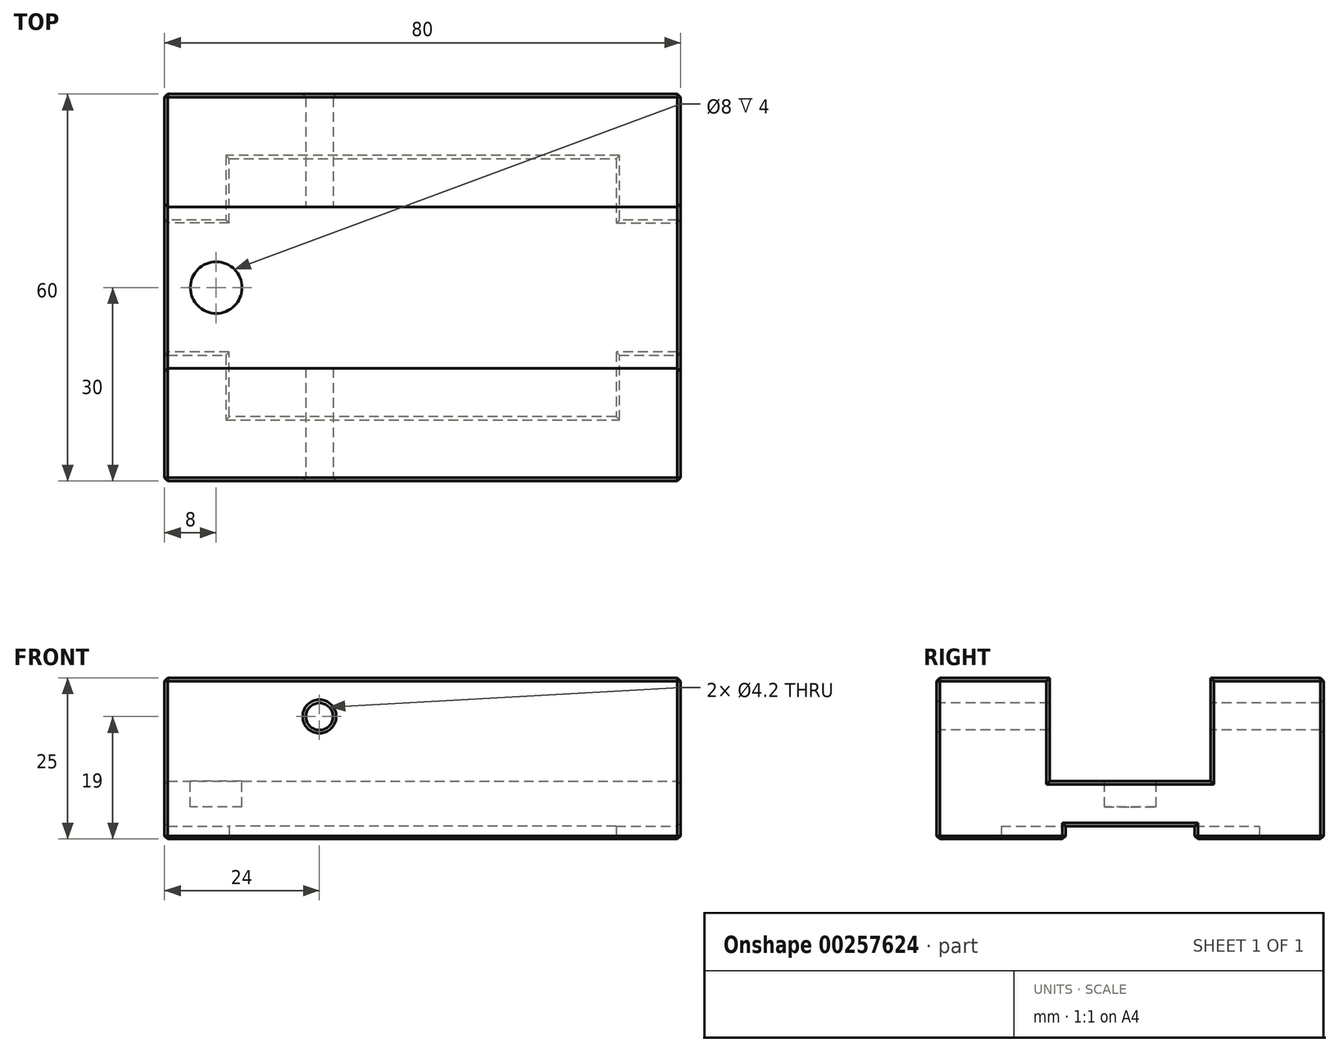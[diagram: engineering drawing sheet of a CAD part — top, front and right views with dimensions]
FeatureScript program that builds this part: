
annotation { "Feature Type Name" : "Feature", "Feature Type Description" : "" }
export const myFeature = defineFeature(function(context is Context, id is Id, definition is map)
    precondition{}
    {
        {
            var Q0;
            Q0=qCreatedBy(makeId("Top.planeOp"),FACE);
            var sketch = newSketch(context, id + "F0", { "sketchPlane" : qUnion([Q0])});
            skLineSegment(sketch, "E0.bottom", {"start": v(40, 30) * mm, "end": v(-40, 30) * mm});
            skLineSegment(sketch, "E0.top", {"start": v(40, -30) * mm, "end": v(-40, -30) * mm});
            skLineSegment(sketch, "E0.left", {"start": v(40, 30) * mm, "end": v(40, -30) * mm});
            skLineSegment(sketch, "E0.right", {"start": v(-40, 30) * mm, "end": v(-40, -30) * mm});
            skPoint(sketch, "E0.middle", {"position": v(0, 0) * mm});
            skSolve(sketch);
        }
        {
            var Q0;
            Q0 = qSketchRegion(id + "F0", true);
            extrude(context, id + "F1", {"entities" : qUnion([Q0]), "depth" : 25 * mm});
        }
        {
            var Q0;
            Q0=makeQuery(id+"F1.opExtrude","CAP_FACE",FACE,{"disambiguationData":[OSD([sQuery(id+"F0.wireOp",EDGE,"E0.bottom"),sQuery(id+"F0.wireOp",EDGE,"E0.top"),sQuery(id+"F0.wireOp",EDGE,"E0.left"),sQuery(id+"F0.wireOp",EDGE,"E0.right")])],"isStart":true});
            var sketch = newSketch(context, id + "F2", { "sketchPlane" : qUnion([Q0])});
            skLineSegment(sketch, "E1.bottom", {"start": v(30, 20) * mm, "end": v(-30, 20) * mm});
            skLineSegment(sketch, "E1.top", {"start": v(30, -20) * mm, "end": v(-30, -20) * mm});
            skLineSegment(sketch, "E1.left", {"start": v(30, 20) * mm, "end": v(30, 10) * mm});
            skLineSegment(sketch, "E1.right", {"start": v(-30, 20) * mm, "end": v(-30, 10) * mm});
            skPoint(sketch, "E1.middle", {"position": v(0, 0) * mm});
            skLineSegment(sketch, "E2", {"start": v(-30, -10) * mm, "end": v(-40, -10) * mm});
            skLineSegment(sketch, "E3", {"start": v(-40, -10) * mm, "end": v(-40, 10) * mm});
            skLineSegment(sketch, "E4", {"start": v(-40, 10) * mm, "end": v(-30, 10) * mm});
            skLineSegment(sketch, "E5.trimOffspring", {"start": v(-30, -10) * mm, "end": v(-30, -20) * mm});
            skLineSegment(sketch, "E6", {"start": v(-30, -10) * mm, "end": v(30, -10) * mm, "construction": true});
            skLineSegment(sketch, "E7", {"start": v(-30, 10) * mm, "end": v(30, 10) * mm, "construction": true});
            skLineSegment(sketch, "E8", {"start": v(30, -10) * mm, "end": v(40, -10) * mm});
            skLineSegment(sketch, "E9", {"start": v(40, -10) * mm, "end": v(40, 10) * mm});
            skLineSegment(sketch, "E10", {"start": v(40, 10) * mm, "end": v(30, 10) * mm});
            skLineSegment(sketch, "E11.trimOffspring", {"start": v(30, -10) * mm, "end": v(30, -20) * mm});
            skSolve(sketch);
        }
        {
            var Q0;
            Q0 = qSketchRegion(id + "F2", true);
            extrude(context, id + "F3", {"entities" : qUnion([Q0]), "operationType" : NewBodyOperationType.REMOVE, "oppositeDirection" : true, "depth" : 2 * mm});
        }
        {
            var Q0;
            Q0=makeQuery(id+"F1.opExtrude","CAP_FACE",FACE,{"disambiguationData":[OSD([sQuery(id+"F0.wireOp",EDGE,"E0.bottom"),sQuery(id+"F0.wireOp",EDGE,"E0.top"),sQuery(id+"F0.wireOp",EDGE,"E0.left"),sQuery(id+"F0.wireOp",EDGE,"E0.right")])],"isStart":false});
            var sketch = newSketch(context, id + "F4", { "sketchPlane" : qUnion([Q0])});
            skLineSegment(sketch, "E12.bottom", {"start": v(-40, -12.5) * mm, "end": v(40, -12.5) * mm});
            skLineSegment(sketch, "E12.top", {"start": v(-40, 12.5) * mm, "end": v(40, 12.5) * mm});
            skLineSegment(sketch, "E12.left", {"start": v(-40, -12.5) * mm, "end": v(-40, 12.5) * mm});
            skLineSegment(sketch, "E12.right", {"start": v(40, -12.5) * mm, "end": v(40, 12.5) * mm});
            skPoint(sketch, "E12.middle", {"position": v(0, 0) * mm});
            skSolve(sketch);
        }
        {
            var Q0;
            Q0=makeQuery(id+"F4.imprint","IMPRINT",FACE,{"disambiguationData":[TD([[makeQuery(id+"F4.imprint","IMPRINT",EDGE,{"derivedFrom":sQuery(id+"F4.wireOp",EDGE,"E12.bottom")}),1.0]])]});
            extrude(context, id + "F5", {"entities" : qUnion([Q0]), "operationType" : NewBodyOperationType.REMOVE, "oppositeDirection" : true, "depth" : 16 * mm});
        }
        {
            var Q0;
            Q0=makeQuery(id+"F5.boolean.opBoolean","COPY",FACE,{"derivedFrom":makeQuery(id+"F5.opExtrude","CAP_FACE",FACE,{"disambiguationData":[OSD([sQuery(id+"F4.wireOp",EDGE,"E12.bottom"),sQuery(id+"F4.wireOp",EDGE,"E12.top"),sQuery(id+"F4.wireOp",EDGE,"E12.left"),sQuery(id+"F4.wireOp",EDGE,"E12.right")])],"isStart":false})});
            var sketch = newSketch(context, id + "F6", { "sketchPlane" : qUnion([Q0])});
            skPoint(sketch, "E13", {"position": v(-32, 0) * mm});
            skCircle(sketch, "E14", {"center": v(-32, 0) * mm, "radius": 4 * mm});
            skSolve(sketch);
        }
        {
            var Q0;
            Q0 = qSketchRegion(id + "F6", true);
            extrude(context, id + "F7", {"entities" : qUnion([Q0]), "operationType" : NewBodyOperationType.REMOVE, "oppositeDirection" : true, "depth" : 4 * mm});
        }
        {
            var Q0;
            Q0=makeQuery(id+"F1.opExtrude","SWEPT_FACE",FACE,{"disambiguationData":[OSD([sQuery(id+"F0.wireOp",EDGE,"E0.top")])]});
            var sketch = newSketch(context, id + "F8", { "sketchPlane" : qUnion([Q0])});
            skLineSegment(sketch, "E15", {"start": v(-40, 9) * mm, "end": v(40, 9) * mm, "construction": true});
            skLineSegment(sketch, "E16", {"start": v(-16, 25) * mm, "end": v(-16, 19) * mm, "construction": true});
            skLineSegment(sketch, "E17", {"start": v(-16, 19) * mm, "end": v(-16, 9) * mm, "construction": true});
            skPoint(sketch, "E18", {"position": v(-16, 19) * mm});
            skSolve(sketch);
        }
        {
            var Q0;
            Q0=sQuery(id+"F8.wireOp",VERTEX,"E18");
            var Q1;
            Q1=makeQuery(id+"F1.opExtrude","SWEPT_BODY",BODY,{"disambiguationData":[OSD([sQuery(id+"F0.wireOp",EDGE,"E0.bottom"),sQuery(id+"F0.wireOp",EDGE,"E0.top"),sQuery(id+"F0.wireOp",EDGE,"E0.left"),sQuery(id+"F0.wireOp",EDGE,"E0.right")])]});
            hole(context, id + "F9", {"style" : HoleStyle.SIMPLE, "endStyle" : HoleEndStyle.THROUGH, "standardTappedOrClearance" : lookupTablePath({ "standard" : "ISO", "engagement" : "75%", "pitch" : "0.8 mm", "size" : "M5", "type" : "Tapped" }), "standardBlindInLast" : lookupTablePath({ "standard" : "ISO", "engagement" : "75%", "pitch" : "0.8 mm", "size" : "M5", "type" : "Tapped" }), "holeDiameter" : 4.2 * mm, "showTappedDepth" : true, "tappedDepth" : 12 * mm, "tapClearance" : 3, "locations" : qUnion([Q0]), "scope" : qUnion([Q1]), "majorDiameter" : 5 * mm});
        }
        {
            var Q0;
            {var subQ0=sQuery(id+"F0.wireOp",EDGE,"E0.right");var subQ1=sQuery(id+"F0.wireOp",EDGE,"E0.left");var subQ2=sQuery(id+"F0.wireOp",EDGE,"E0.bottom");Q0=makeQuery(id+"F3.boolean.opBoolean","SPLIT",FACE,{"disambiguationData":[TD([makeQuery(id+"F1.opExtrude","SWEPT_FACE",FACE,{"disambiguationData":[OSD([subQ2])]})])],"derivedFrom":makeQuery(id+"F1.opExtrude","CAP_FACE",FACE,{"disambiguationData":[OSD([subQ2,sQuery(id+"F0.wireOp",EDGE,"E0.top"),subQ1,subQ0])],"isStart":true})});}
            var Q1;
            {var subQ0=sQuery(id+"F0.wireOp",EDGE,"E0.right");var subQ1=sQuery(id+"F0.wireOp",EDGE,"E0.left");var subQ2=sQuery(id+"F0.wireOp",EDGE,"E0.top");Q1=makeQuery(id+"F3.boolean.opBoolean","SPLIT",FACE,{"disambiguationData":[TD([makeQuery(id+"F1.opExtrude","SWEPT_FACE",FACE,{"disambiguationData":[OSD([subQ2])]})])],"derivedFrom":makeQuery(id+"F1.opExtrude","CAP_FACE",FACE,{"disambiguationData":[OSD([sQuery(id+"F0.wireOp",EDGE,"E0.bottom"),subQ2,subQ1,subQ0])],"isStart":true})});}
            var Q2;
            Q2=makeQuery(id+"F1.opExtrude","SWEPT_FACE",FACE,{"disambiguationData":[OSD([sQuery(id+"F0.wireOp",EDGE,"E0.right")])]});
            var Q3;
            Q3=makeQuery(id+"F1.opExtrude","SWEPT_FACE",FACE,{"disambiguationData":[OSD([sQuery(id+"F0.wireOp",EDGE,"E0.top")])]});
            var Q4;
            Q4=makeQuery(id+"F1.opExtrude","SWEPT_FACE",FACE,{"disambiguationData":[OSD([sQuery(id+"F0.wireOp",EDGE,"E0.left")])]});
            var Q5;
            Q5=makeQuery(id+"F1.opExtrude","SWEPT_FACE",FACE,{"disambiguationData":[OSD([sQuery(id+"F0.wireOp",EDGE,"E0.bottom")])]});
            chamfer(context, id + "F10", {"entities" : qUnion([Q0, Q1, Q2, Q3, Q4, Q5]), "width" : .5 * mm, "tangentPropagation" : true});
        }
    });
